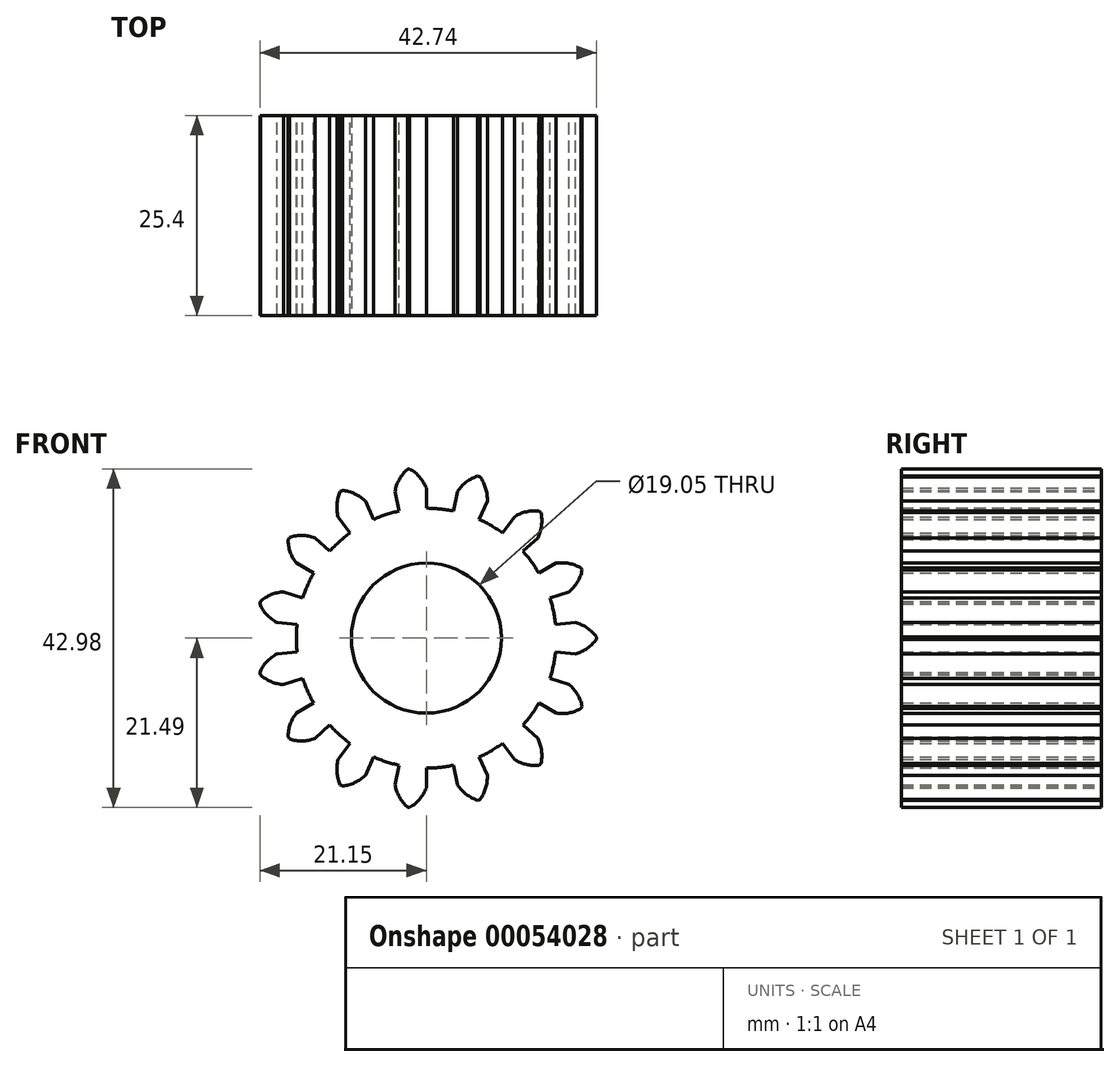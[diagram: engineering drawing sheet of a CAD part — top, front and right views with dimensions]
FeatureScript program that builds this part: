
annotation { "Feature Type Name" : "Feature", "Feature Type Description" : "" }
export const myFeature = defineFeature(function(context is Context, id is Id, definition is map)
    precondition{}
    {
        {
            var Q0;
            Q0=qCreatedBy(makeId("Front.planeOp"),FACE);
            var sketch = newSketch(context, id + "F0", { "sketchPlane" : qUnion([Q0])});
            skArc(sketch, "E0", {"start": v(-3.43, 16.15) * mm, "mid": v(-5.1, 15.7) * mm, "end": v(-6.72, 15.08) * mm});
            skArc(sketch, "E1", {"start": v(0, 19.05) * mm, "mid": v(-0.84, 20.45) * mm, "end": v(-2.1, 21.49) * mm});
            skLineSegment(sketch, "E2", {"start": v(0, 19.05) * mm, "end": v(0, 16.51) * mm});
            skLineSegment(sketch, "E3", {"start": v(-2.1, 21.49) * mm, "end": v(-2.26, 21.47) * mm});
            skLineSegment(sketch, "E4.MirrorCS", {"start": v(-2.41, 21.46) * mm, "end": v(-2.26, 21.47) * mm});
            skArc(sketch, "E5.MirrorCS", {"start": v(-3.96, 18.63) * mm, "mid": v(-3.43, 20.18) * mm, "end": v(-2.41, 21.46) * mm});
            skLineSegment(sketch, "E6.MirrorCS", {"start": v(-3.96, 18.63) * mm, "end": v(-3.43, 16.15) * mm});
            skLineSegment(sketch, "E7.1.0", {"start": v(-10.66, 18.77) * mm, "end": v(-10.8, 18.7) * mm});
            skLineSegment(sketch, "E7.1.1", {"start": v(-10.93, 18.62) * mm, "end": v(-10.8, 18.7) * mm});
            skArc(sketch, "E7.1.2", {"start": v(-11.2, 15.41) * mm, "mid": v(-11.34, 17.04) * mm, "end": v(-10.93, 18.62) * mm});
            skArc(sketch, "E7.1.3", {"start": v(-7.75, 17.4) * mm, "mid": v(-9.09, 18.34) * mm, "end": v(-10.66, 18.77) * mm});
            skLineSegment(sketch, "E7.1.4", {"start": v(-7.75, 17.4) * mm, "end": v(-6.72, 15.08) * mm});
            skLineSegment(sketch, "E7.1.5", {"start": v(-11.2, 15.41) * mm, "end": v(-9.7, 13.36) * mm});
            skLineSegment(sketch, "E7.2.0", {"start": v(-17.38, 12.81) * mm, "end": v(-17.47, 12.7) * mm});
            skLineSegment(sketch, "E7.2.1", {"start": v(-17.56, 12.56) * mm, "end": v(-17.47, 12.7) * mm});
            skArc(sketch, "E7.2.2", {"start": v(-16.5, 9.53) * mm, "mid": v(-17.3, 10.95) * mm, "end": v(-17.56, 12.56) * mm});
            skArc(sketch, "E7.2.3", {"start": v(-14.16, 12.75) * mm, "mid": v(-15.76, 13.06) * mm, "end": v(-17.38, 12.81) * mm});
            skLineSegment(sketch, "E7.2.4", {"start": v(-14.16, 12.75) * mm, "end": v(-12.27, 11.05) * mm});
            skLineSegment(sketch, "E7.2.5", {"start": v(-16.5, 9.53) * mm, "end": v(-14.3, 8.26) * mm});
            skLineSegment(sketch, "E7.3.0", {"start": v(-21.09, 4.64) * mm, "end": v(-21.12, 4.49) * mm});
            skLineSegment(sketch, "E7.3.1", {"start": v(-21.15, 4.34) * mm, "end": v(-21.12, 4.49) * mm});
            skArc(sketch, "E7.3.2", {"start": v(-18.95, 2) * mm, "mid": v(-20.25, 2.97) * mm, "end": v(-21.15, 4.34) * mm});
            skArc(sketch, "E7.3.3", {"start": v(-18.12, 5.89) * mm, "mid": v(-19.71, 5.52) * mm, "end": v(-21.09, 4.64) * mm});
            skLineSegment(sketch, "E7.3.4", {"start": v(-18.12, 5.89) * mm, "end": v(-15.7, 5.1) * mm});
            skLineSegment(sketch, "E7.3.5", {"start": v(-18.95, 2) * mm, "end": v(-16.42, 1.73) * mm});
            skLineSegment(sketch, "E7.4.0", {"start": v(-21.15, -4.34) * mm, "end": v(-21.12, -4.49) * mm});
            skLineSegment(sketch, "E7.4.1", {"start": v(-21.09, -4.64) * mm, "end": v(-21.12, -4.49) * mm});
            skArc(sketch, "E7.4.2", {"start": v(-18.12, -5.89) * mm, "mid": v(-19.71, -5.52) * mm, "end": v(-21.09, -4.64) * mm});
            skArc(sketch, "E7.4.3", {"start": v(-18.95, -2) * mm, "mid": v(-20.25, -2.97) * mm, "end": v(-21.15, -4.34) * mm});
            skLineSegment(sketch, "E7.4.4", {"start": v(-18.95, -2) * mm, "end": v(-16.42, -1.73) * mm});
            skLineSegment(sketch, "E7.4.5", {"start": v(-18.12, -5.89) * mm, "end": v(-15.7, -5.1) * mm});
            skLineSegment(sketch, "E7.5.0", {"start": v(-17.56, -12.56) * mm, "end": v(-17.47, -12.7) * mm});
            skLineSegment(sketch, "E7.5.1", {"start": v(-17.38, -12.81) * mm, "end": v(-17.47, -12.7) * mm});
            skArc(sketch, "E7.5.2", {"start": v(-14.16, -12.75) * mm, "mid": v(-15.76, -13.06) * mm, "end": v(-17.38, -12.81) * mm});
            skArc(sketch, "E7.5.3", {"start": v(-16.5, -9.52) * mm, "mid": v(-17.3, -10.95) * mm, "end": v(-17.56, -12.56) * mm});
            skLineSegment(sketch, "E7.5.4", {"start": v(-16.5, -9.52) * mm, "end": v(-14.3, -8.25) * mm});
            skLineSegment(sketch, "E7.5.5", {"start": v(-14.16, -12.75) * mm, "end": v(-12.27, -11.05) * mm});
            skLineSegment(sketch, "E7.6.0", {"start": v(-10.93, -18.62) * mm, "end": v(-10.8, -18.7) * mm});
            skLineSegment(sketch, "E7.6.1", {"start": v(-10.66, -18.77) * mm, "end": v(-10.8, -18.7) * mm});
            skArc(sketch, "E7.6.2", {"start": v(-7.75, -17.4) * mm, "mid": v(-9.09, -18.34) * mm, "end": v(-10.66, -18.77) * mm});
            skArc(sketch, "E7.6.3", {"start": v(-11.2, -15.41) * mm, "mid": v(-11.34, -17.04) * mm, "end": v(-10.93, -18.62) * mm});
            skLineSegment(sketch, "E7.6.4", {"start": v(-11.2, -15.41) * mm, "end": v(-9.7, -13.36) * mm});
            skLineSegment(sketch, "E7.6.5", {"start": v(-7.75, -17.4) * mm, "end": v(-6.72, -15.08) * mm});
            skLineSegment(sketch, "E7.7.0", {"start": v(-2.41, -21.46) * mm, "end": v(-2.26, -21.47) * mm});
            skLineSegment(sketch, "E7.7.1", {"start": v(-2.1, -21.49) * mm, "end": v(-2.26, -21.47) * mm});
            skArc(sketch, "E7.7.2", {"start": v(0, -19.05) * mm, "mid": v(-0.84, -20.45) * mm, "end": v(-2.1, -21.49) * mm});
            skArc(sketch, "E7.7.3", {"start": v(-3.96, -18.63) * mm, "mid": v(-3.43, -20.18) * mm, "end": v(-2.41, -21.46) * mm});
            skLineSegment(sketch, "E7.7.4", {"start": v(-3.96, -18.63) * mm, "end": v(-3.43, -16.15) * mm});
            skLineSegment(sketch, "E7.7.5", {"start": v(0, -19.05) * mm, "end": v(0, -16.51) * mm});
            skLineSegment(sketch, "E7.8.0", {"start": v(6.52, -20.58) * mm, "end": v(6.67, -20.53) * mm});
            skLineSegment(sketch, "E7.8.1", {"start": v(6.82, -20.49) * mm, "end": v(6.67, -20.53) * mm});
            skArc(sketch, "E7.8.2", {"start": v(7.75, -17.4) * mm, "mid": v(7.55, -19.03) * mm, "end": v(6.82, -20.49) * mm});
            skArc(sketch, "E7.8.3", {"start": v(3.96, -18.63) * mm, "mid": v(5.07, -19.83) * mm, "end": v(6.52, -20.58) * mm});
            skLineSegment(sketch, "E7.8.4", {"start": v(3.96, -18.63) * mm, "end": v(3.43, -16.15) * mm});
            skLineSegment(sketch, "E7.8.5", {"start": v(7.75, -17.4) * mm, "end": v(6.72, -15.08) * mm});
            skLineSegment(sketch, "E7.9.0", {"start": v(14.33, -16.15) * mm, "end": v(14.45, -16.04) * mm});
            skLineSegment(sketch, "E7.9.1", {"start": v(14.56, -15.94) * mm, "end": v(14.45, -16.04) * mm});
            skArc(sketch, "E7.9.2", {"start": v(14.16, -12.75) * mm, "mid": v(14.64, -14.3) * mm, "end": v(14.56, -15.94) * mm});
            skArc(sketch, "E7.9.3", {"start": v(11.2, -15.41) * mm, "mid": v(12.7, -16.05) * mm, "end": v(14.33, -16.15) * mm});
            skLineSegment(sketch, "E7.9.4", {"start": v(11.2, -15.41) * mm, "end": v(9.7, -13.36) * mm});
            skLineSegment(sketch, "E7.9.5", {"start": v(14.16, -12.75) * mm, "end": v(12.27, -11.05) * mm});
            skLineSegment(sketch, "E7.10.0", {"start": v(19.66, -8.92) * mm, "end": v(19.72, -8.78) * mm});
            skLineSegment(sketch, "E7.10.1", {"start": v(19.79, -8.64) * mm, "end": v(19.72, -8.78) * mm});
            skArc(sketch, "E7.10.2", {"start": v(18.12, -5.89) * mm, "mid": v(19.2, -7.12) * mm, "end": v(19.79, -8.64) * mm});
            skArc(sketch, "E7.10.3", {"start": v(16.5, -9.53) * mm, "mid": v(18.13, -9.5) * mm, "end": v(19.66, -8.92) * mm});
            skLineSegment(sketch, "E7.10.4", {"start": v(16.5, -9.53) * mm, "end": v(14.3, -8.26) * mm});
            skLineSegment(sketch, "E7.10.5", {"start": v(18.12, -5.89) * mm, "end": v(15.7, -5.1) * mm});
            skLineSegment(sketch, "E7.11.0", {"start": v(21.59, -0.15) * mm, "end": v(21.6, 0) * mm});
            skLineSegment(sketch, "E7.11.1", {"start": v(21.59, 0.15) * mm, "end": v(21.6, 0) * mm});
            skArc(sketch, "E7.11.2", {"start": v(18.95, 2) * mm, "mid": v(20.43, 1.3) * mm, "end": v(21.59, 0.15) * mm});
            skArc(sketch, "E7.11.3", {"start": v(18.95, -2) * mm, "mid": v(20.43, -1.3) * mm, "end": v(21.59, -0.15) * mm});
            skLineSegment(sketch, "E7.11.4", {"start": v(18.95, -2) * mm, "end": v(16.42, -1.73) * mm});
            skLineSegment(sketch, "E7.11.5", {"start": v(18.95, 2) * mm, "end": v(16.42, 1.73) * mm});
            skLineSegment(sketch, "E7.12.0", {"start": v(19.79, 8.64) * mm, "end": v(19.72, 8.78) * mm});
            skLineSegment(sketch, "E7.12.1", {"start": v(19.66, 8.92) * mm, "end": v(19.72, 8.78) * mm});
            skArc(sketch, "E7.12.2", {"start": v(16.5, 9.52) * mm, "mid": v(18.13, 9.5) * mm, "end": v(19.66, 8.92) * mm});
            skArc(sketch, "E7.12.3", {"start": v(18.12, 5.89) * mm, "mid": v(19.2, 7.12) * mm, "end": v(19.79, 8.64) * mm});
            skLineSegment(sketch, "E7.12.4", {"start": v(18.12, 5.89) * mm, "end": v(15.7, 5.1) * mm});
            skLineSegment(sketch, "E7.12.5", {"start": v(16.5, 9.52) * mm, "end": v(14.3, 8.25) * mm});
            skLineSegment(sketch, "E7.13.0", {"start": v(14.56, 15.94) * mm, "end": v(14.45, 16.04) * mm});
            skLineSegment(sketch, "E7.13.1", {"start": v(14.33, 16.15) * mm, "end": v(14.45, 16.04) * mm});
            skArc(sketch, "E7.13.2", {"start": v(11.2, 15.41) * mm, "mid": v(12.7, 16.05) * mm, "end": v(14.33, 16.15) * mm});
            skArc(sketch, "E7.13.3", {"start": v(14.16, 12.75) * mm, "mid": v(14.64, 14.3) * mm, "end": v(14.56, 15.94) * mm});
            skLineSegment(sketch, "E7.13.4", {"start": v(14.16, 12.75) * mm, "end": v(12.27, 11.05) * mm});
            skLineSegment(sketch, "E7.13.5", {"start": v(11.2, 15.41) * mm, "end": v(9.7, 13.36) * mm});
            skLineSegment(sketch, "E7.14.0", {"start": v(6.82, 20.49) * mm, "end": v(6.67, 20.53) * mm});
            skLineSegment(sketch, "E7.14.1", {"start": v(6.52, 20.58) * mm, "end": v(6.67, 20.53) * mm});
            skArc(sketch, "E7.14.2", {"start": v(3.96, 18.63) * mm, "mid": v(5.07, 19.83) * mm, "end": v(6.52, 20.58) * mm});
            skArc(sketch, "E7.14.3", {"start": v(7.75, 17.4) * mm, "mid": v(7.55, 19.03) * mm, "end": v(6.82, 20.49) * mm});
            skLineSegment(sketch, "E7.14.4", {"start": v(7.75, 17.4) * mm, "end": v(6.72, 15.08) * mm});
            skLineSegment(sketch, "E7.14.5", {"start": v(3.96, 18.63) * mm, "end": v(3.43, 16.15) * mm});
            skArc(sketch, "E8.trimOffspring", {"start": v(3.43, 16.15) * mm, "mid": v(1.73, 16.42) * mm, "end": v(0, 16.51) * mm});
            skArc(sketch, "E9.trimOffspring", {"start": v(9.7, 13.36) * mm, "mid": v(8.26, 14.3) * mm, "end": v(6.72, 15.08) * mm});
            skArc(sketch, "E10.trimOffspring", {"start": v(14.3, 8.25) * mm, "mid": v(13.36, 9.7) * mm, "end": v(12.27, 11.05) * mm});
            skArc(sketch, "E11.trimOffspring", {"start": v(16.42, 1.73) * mm, "mid": v(16.15, 3.43) * mm, "end": v(15.7, 5.1) * mm});
            skArc(sketch, "E12.trimOffspring", {"start": v(15.7, -5.1) * mm, "mid": v(16.15, -3.43) * mm, "end": v(16.42, -1.73) * mm});
            skArc(sketch, "E13.trimOffspring", {"start": v(12.27, -11.05) * mm, "mid": v(13.36, -9.7) * mm, "end": v(14.3, -8.26) * mm});
            skArc(sketch, "E14.trimOffspring", {"start": v(6.72, -15.08) * mm, "mid": v(8.25, -14.3) * mm, "end": v(9.7, -13.36) * mm});
            skArc(sketch, "E15.trimOffspring", {"start": v(0, -16.51) * mm, "mid": v(1.73, -16.42) * mm, "end": v(3.43, -16.15) * mm});
            skArc(sketch, "E16.trimOffspring", {"start": v(-6.72, -15.08) * mm, "mid": v(-5.1, -15.7) * mm, "end": v(-3.43, -16.15) * mm});
            skArc(sketch, "E17.trimOffspring", {"start": v(-12.27, -11.05) * mm, "mid": v(-11.05, -12.27) * mm, "end": v(-9.7, -13.36) * mm});
            skArc(sketch, "E18.trimOffspring", {"start": v(-15.7, -5.1) * mm, "mid": v(-15.08, -6.72) * mm, "end": v(-14.3, -8.25) * mm});
            skArc(sketch, "E19.trimOffspring", {"start": v(-16.42, 1.73) * mm, "mid": v(-16.51, 0) * mm, "end": v(-16.42, -1.73) * mm});
            skArc(sketch, "E20.trimOffspring", {"start": v(-14.3, 8.26) * mm, "mid": v(-15.08, 6.72) * mm, "end": v(-15.7, 5.1) * mm});
            skArc(sketch, "E21.trimOffspring", {"start": v(-9.7, 13.36) * mm, "mid": v(-11.05, 12.27) * mm, "end": v(-12.27, 11.05) * mm});
            skSolve(sketch);
        }
        {
            var Q0;
            Q0 = qSketchRegion(id + "F0", true);
            extrude(context, id + "F1", {"entities" : qUnion([Q0]), "depth" : 25.4 * mm});
        }
        {
            var Q0;
            Q0=makeQuery(id+"F1.opExtrude","CAP_FACE",FACE,{"disambiguationData":[OSD([sQuery(id+"F0.wireOp",EDGE,"E0"),sQuery(id+"F0.wireOp",EDGE,"E1"),sQuery(id+"F0.wireOp",EDGE,"E2"),sQuery(id+"F0.wireOp",EDGE,"E3"),sQuery(id+"F0.wireOp",EDGE,"E4.MirrorCS"),sQuery(id+"F0.wireOp",EDGE,"E5.MirrorCS"),sQuery(id+"F0.wireOp",EDGE,"E6.MirrorCS"),sQuery(id+"F0.wireOp",EDGE,"E7.1.0"),sQuery(id+"F0.wireOp",EDGE,"E7.1.1"),sQuery(id+"F0.wireOp",EDGE,"E7.1.2"),sQuery(id+"F0.wireOp",EDGE,"E7.1.3"),sQuery(id+"F0.wireOp",EDGE,"E7.1.4"),sQuery(id+"F0.wireOp",EDGE,"E7.1.5"),sQuery(id+"F0.wireOp",EDGE,"E7.2.0"),sQuery(id+"F0.wireOp",EDGE,"E7.2.1"),sQuery(id+"F0.wireOp",EDGE,"E7.2.2"),sQuery(id+"F0.wireOp",EDGE,"E7.2.3"),sQuery(id+"F0.wireOp",EDGE,"E7.2.4"),sQuery(id+"F0.wireOp",EDGE,"E7.2.5"),sQuery(id+"F0.wireOp",EDGE,"E7.3.0"),sQuery(id+"F0.wireOp",EDGE,"E7.3.1"),sQuery(id+"F0.wireOp",EDGE,"E7.3.2"),sQuery(id+"F0.wireOp",EDGE,"E7.3.3"),sQuery(id+"F0.wireOp",EDGE,"E7.3.4"),sQuery(id+"F0.wireOp",EDGE,"E7.3.5"),sQuery(id+"F0.wireOp",EDGE,"E7.4.0"),sQuery(id+"F0.wireOp",EDGE,"E7.4.1"),sQuery(id+"F0.wireOp",EDGE,"E7.4.2"),sQuery(id+"F0.wireOp",EDGE,"E7.4.3"),sQuery(id+"F0.wireOp",EDGE,"E7.4.4"),sQuery(id+"F0.wireOp",EDGE,"E7.4.5"),sQuery(id+"F0.wireOp",EDGE,"E7.5.0"),sQuery(id+"F0.wireOp",EDGE,"E7.5.1"),sQuery(id+"F0.wireOp",EDGE,"E7.5.2"),sQuery(id+"F0.wireOp",EDGE,"E7.5.3"),sQuery(id+"F0.wireOp",EDGE,"E7.5.4"),sQuery(id+"F0.wireOp",EDGE,"E7.5.5"),sQuery(id+"F0.wireOp",EDGE,"E7.6.0"),sQuery(id+"F0.wireOp",EDGE,"E7.6.1"),sQuery(id+"F0.wireOp",EDGE,"E7.6.2"),sQuery(id+"F0.wireOp",EDGE,"E7.6.3"),sQuery(id+"F0.wireOp",EDGE,"E7.6.4"),sQuery(id+"F0.wireOp",EDGE,"E7.6.5"),sQuery(id+"F0.wireOp",EDGE,"E7.7.0"),sQuery(id+"F0.wireOp",EDGE,"E7.7.1"),sQuery(id+"F0.wireOp",EDGE,"E7.7.2"),sQuery(id+"F0.wireOp",EDGE,"E7.7.3"),sQuery(id+"F0.wireOp",EDGE,"E7.7.4"),sQuery(id+"F0.wireOp",EDGE,"E7.7.5"),sQuery(id+"F0.wireOp",EDGE,"E7.8.0"),sQuery(id+"F0.wireOp",EDGE,"E7.8.1"),sQuery(id+"F0.wireOp",EDGE,"E7.8.2"),sQuery(id+"F0.wireOp",EDGE,"E7.8.3"),sQuery(id+"F0.wireOp",EDGE,"E7.8.4"),sQuery(id+"F0.wireOp",EDGE,"E7.8.5"),sQuery(id+"F0.wireOp",EDGE,"E7.9.0"),sQuery(id+"F0.wireOp",EDGE,"E7.9.1"),sQuery(id+"F0.wireOp",EDGE,"E7.9.2"),sQuery(id+"F0.wireOp",EDGE,"E7.9.3"),sQuery(id+"F0.wireOp",EDGE,"E7.9.4"),sQuery(id+"F0.wireOp",EDGE,"E7.9.5"),sQuery(id+"F0.wireOp",EDGE,"E7.10.0"),sQuery(id+"F0.wireOp",EDGE,"E7.10.1"),sQuery(id+"F0.wireOp",EDGE,"E7.10.2"),sQuery(id+"F0.wireOp",EDGE,"E7.10.3"),sQuery(id+"F0.wireOp",EDGE,"E7.10.4"),sQuery(id+"F0.wireOp",EDGE,"E7.10.5"),sQuery(id+"F0.wireOp",EDGE,"E7.11.0"),sQuery(id+"F0.wireOp",EDGE,"E7.11.1"),sQuery(id+"F0.wireOp",EDGE,"E7.11.2"),sQuery(id+"F0.wireOp",EDGE,"E7.11.3"),sQuery(id+"F0.wireOp",EDGE,"E7.11.4"),sQuery(id+"F0.wireOp",EDGE,"E7.11.5"),sQuery(id+"F0.wireOp",EDGE,"E7.12.0"),sQuery(id+"F0.wireOp",EDGE,"E7.12.1"),sQuery(id+"F0.wireOp",EDGE,"E7.12.2"),sQuery(id+"F0.wireOp",EDGE,"E7.12.3"),sQuery(id+"F0.wireOp",EDGE,"E7.12.4"),sQuery(id+"F0.wireOp",EDGE,"E7.12.5"),sQuery(id+"F0.wireOp",EDGE,"E7.13.0"),sQuery(id+"F0.wireOp",EDGE,"E7.13.1"),sQuery(id+"F0.wireOp",EDGE,"E7.13.2"),sQuery(id+"F0.wireOp",EDGE,"E7.13.3"),sQuery(id+"F0.wireOp",EDGE,"E7.13.4"),sQuery(id+"F0.wireOp",EDGE,"E7.13.5"),sQuery(id+"F0.wireOp",EDGE,"E7.14.0"),sQuery(id+"F0.wireOp",EDGE,"E7.14.1"),sQuery(id+"F0.wireOp",EDGE,"E7.14.2"),sQuery(id+"F0.wireOp",EDGE,"E7.14.3"),sQuery(id+"F0.wireOp",EDGE,"E7.14.4"),sQuery(id+"F0.wireOp",EDGE,"E7.14.5"),sQuery(id+"F0.wireOp",EDGE,"E8.trimOffspring"),sQuery(id+"F0.wireOp",EDGE,"E9.trimOffspring"),sQuery(id+"F0.wireOp",EDGE,"E10.trimOffspring"),sQuery(id+"F0.wireOp",EDGE,"E11.trimOffspring"),sQuery(id+"F0.wireOp",EDGE,"E12.trimOffspring"),sQuery(id+"F0.wireOp",EDGE,"E13.trimOffspring"),sQuery(id+"F0.wireOp",EDGE,"E14.trimOffspring"),sQuery(id+"F0.wireOp",EDGE,"E15.trimOffspring"),sQuery(id+"F0.wireOp",EDGE,"E16.trimOffspring"),sQuery(id+"F0.wireOp",EDGE,"E17.trimOffspring"),sQuery(id+"F0.wireOp",EDGE,"E18.trimOffspring"),sQuery(id+"F0.wireOp",EDGE,"E19.trimOffspring"),sQuery(id+"F0.wireOp",EDGE,"E20.trimOffspring"),sQuery(id+"F0.wireOp",EDGE,"E21.trimOffspring")])],"isStart":false});
            var sketch = newSketch(context, id + "F2", { "sketchPlane" : qUnion([Q0])});
            skCircle(sketch, "E22", {"center": v(0, 0) * mm, "radius": 9.53 * mm});
            skSolve(sketch);
        }
        {
            var Q0;
            Q0 = qSketchRegion(id + "F2", true);
            extrude(context, id + "F3", {"entities" : qUnion([Q0]), "operationType" : NewBodyOperationType.REMOVE, "oppositeDirection" : true, "depth" : 25.4 * mm});
        }
    });
